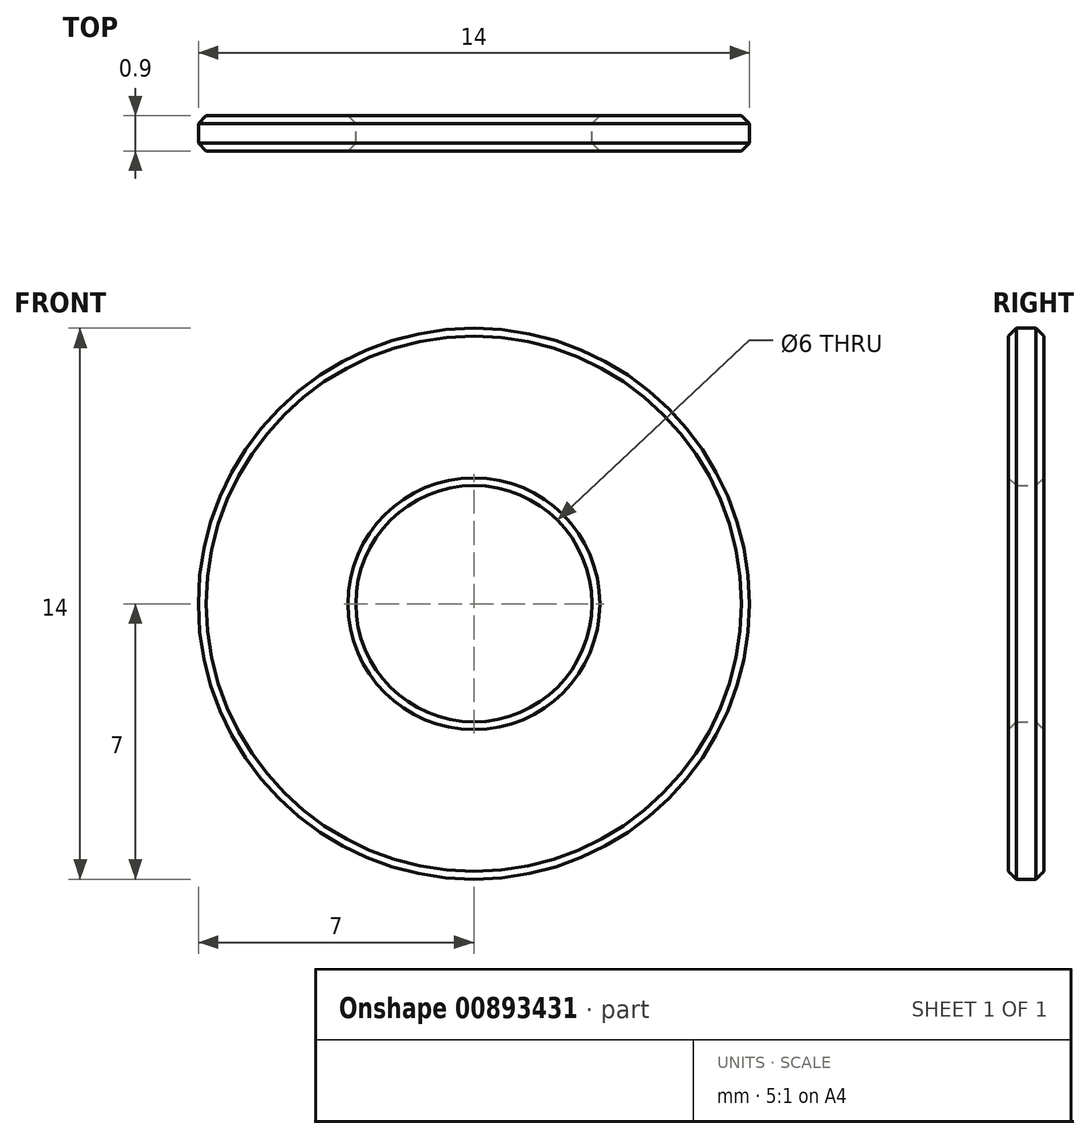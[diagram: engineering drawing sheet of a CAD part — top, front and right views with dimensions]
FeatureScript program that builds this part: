
annotation { "Feature Type Name" : "Feature", "Feature Type Description" : "" }
export const myFeature = defineFeature(function(context is Context, id is Id, definition is map)
    precondition{}
    {
        {
            var Q0;
            Q0=qCreatedBy(makeId("Front.planeOp"),FACE);
            var sketch = newSketch(context, id + "F0", { "sketchPlane" : qUnion([Q0])});
            skCircle(sketch, "E0", {"center": v(0, 0) * mm, "radius": 3 * mm});
            skCircle(sketch, "E1", {"center": v(0, 0) * mm, "radius": 7 * mm});
            skSolve(sketch);
        }
        {
            var Q0;
            Q0=makeQuery(id+"F0.imprint","IMPRINT",FACE,{"disambiguationData":[TD([[makeQuery(id+"F0.imprint","IMPRINT",EDGE,{"derivedFrom":sQuery(id+"F0.wireOp",EDGE,"E0")}),-1.0]])]});
            extrude(context, id + "F1", {"entities" : qUnion([Q0]), "depth" : 0.9 * mm, "offsetDistance" : 25 * mm});
        }
        {
            var Q0;
            Q0=makeQuery(id+"F1.opExtrude","CAP_FACE",FACE,{"disambiguationData":[OSD([sQuery(id+"F0.wireOp",EDGE,"E0"),sQuery(id+"F0.wireOp",EDGE,"E1")])],"isStart":false});
            var Q1;
            Q1=makeQuery(id+"F1.opExtrude","CAP_FACE",FACE,{"disambiguationData":[OSD([sQuery(id+"F0.wireOp",EDGE,"E0"),sQuery(id+"F0.wireOp",EDGE,"E1")])],"isStart":true});
            chamfer(context, id + "F2", {"entities" : qUnion([Q0, Q1]), "width" : 0.2 * mm, "tangentPropagation" : true});
        }
    });
